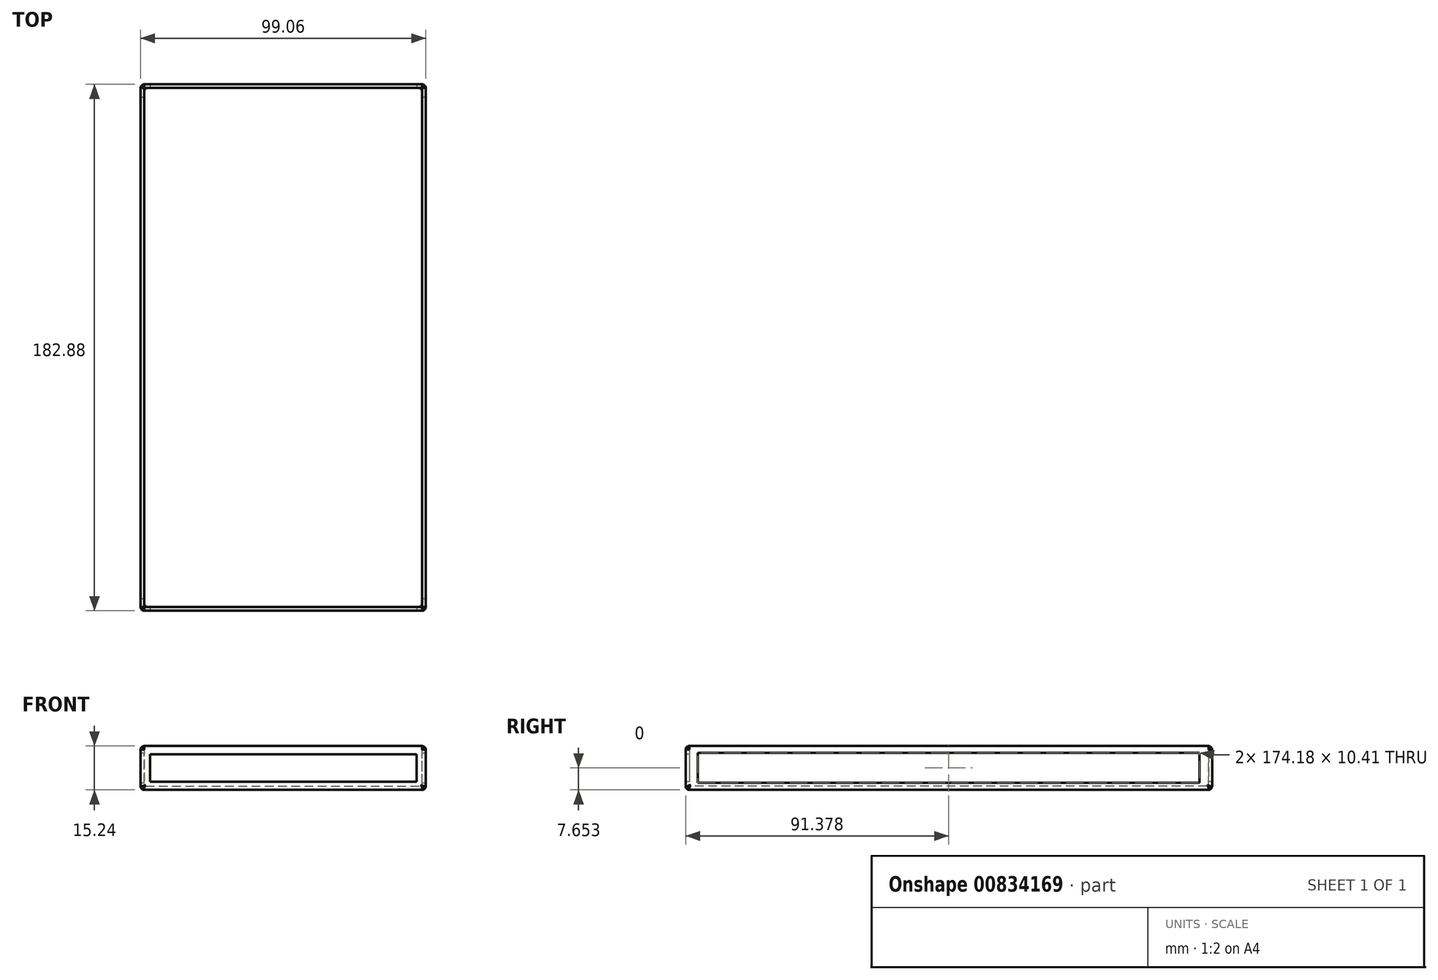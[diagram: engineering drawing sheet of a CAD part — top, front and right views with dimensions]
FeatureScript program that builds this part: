
annotation { "Feature Type Name" : "Feature", "Feature Type Description" : "" }
export const myFeature = defineFeature(function(context is Context, id is Id, definition is map)
    precondition{}
    {
        {
            var Q0;
            Q0=qCreatedBy(makeId("Top.planeOp"),FACE);
            var sketch = newSketch(context, id + "F0", { "sketchPlane" : qUnion([Q0])});
            skLineSegment(sketch, "E0.bottom", {"start": v(-49.53, 91.44) * mm, "end": v(49.53, 91.44) * mm, "construction": true});
            skLineSegment(sketch, "E0.top", {"start": v(-49.53, -91.44) * mm, "end": v(49.53, -91.44) * mm, "construction": true});
            skLineSegment(sketch, "E0.left", {"start": v(-49.53, 91.44) * mm, "end": v(-49.53, -91.44) * mm, "construction": true});
            skLineSegment(sketch, "E0.right", {"start": v(49.53, 91.44) * mm, "end": v(49.53, -91.44) * mm, "construction": true});
            skPoint(sketch, "E0.middle", {"position": v(0, 0) * mm});
            skSolve(sketch);
        }
        {
            var Q0;
            Q0=qCreatedBy(makeId("Top.planeOp"),FACE);
            var sketch = newSketch(context, id + "F1", { "sketchPlane" : qUnion([Q0])});
            skLineSegment(sketch, "E1.bottom", {"start": v(-49.53, 91.44) * mm, "end": v(49.53, 91.44) * mm});
            skLineSegment(sketch, "E1.top", {"start": v(-49.53, -91.44) * mm, "end": v(49.53, -91.44) * mm});
            skLineSegment(sketch, "E1.left", {"start": v(-49.53, 91.44) * mm, "end": v(-49.53, -91.44) * mm});
            skLineSegment(sketch, "E1.right", {"start": v(49.53, 91.44) * mm, "end": v(49.53, -91.44) * mm});
            skSolve(sketch);
        }
        {
            var Q0;
            Q0=qSketchRegion(id+"F1",true);
            extrude(context, id + "F2", {"entities" : qUnion([Q0]), "depth" : 15.24 * mm});
        }
        {
            var Q0;
            Q0=makeQuery(id+"F2.opExtrude","CAP_FACE",FACE,{"disambiguationData":[OSD([sQuery(id+"F1.wireOp",EDGE,"E1.bottom"),sQuery(id+"F1.wireOp",EDGE,"E1.top"),sQuery(id+"F1.wireOp",EDGE,"E1.left"),sQuery(id+"F1.wireOp",EDGE,"E1.right")])],"isStart":false});
            shell(context, id + "F3", {"entities" : qUnion([Q0]), "thickness" : 1.27 * mm});
        }
        {
            var Q0;
            Q0=makeQuery(id+"F2.opExtrude","SWEPT_EDGE",EDGE,{"disambiguationData":[OSD([sQuery(id+"F1.wireOp",EDGE,"E1.bottom"),sQuery(id+"F1.wireOp",EDGE,"E1.right")])]});
            var Q1;
            Q1=makeQuery(id+"F2.opExtrude","SWEPT_EDGE",EDGE,{"disambiguationData":[OSD([sQuery(id+"F1.wireOp",EDGE,"E1.bottom"),sQuery(id+"F1.wireOp",EDGE,"E1.left")])]});
            var Q2;
            Q2=makeQuery(id+"F2.opExtrude","SWEPT_EDGE",EDGE,{"disambiguationData":[OSD([sQuery(id+"F1.wireOp",EDGE,"E1.top"),sQuery(id+"F1.wireOp",EDGE,"E1.left")])]});
            var Q3;
            Q3=makeQuery(id+"F2.opExtrude","SWEPT_EDGE",EDGE,{"disambiguationData":[OSD([sQuery(id+"F1.wireOp",EDGE,"E1.top"),sQuery(id+"F1.wireOp",EDGE,"E1.right")])]});
            var Q4;
            Q4=makeQuery(id+"F2.opExtrude","CAP_EDGE",EDGE,{"disambiguationData":[OSD([sQuery(id+"F1.wireOp",EDGE,"E1.top")])],"isStart":true});
            var Q5;
            Q5=makeQuery(id+"F2.opExtrude","CAP_EDGE",EDGE,{"disambiguationData":[OSD([sQuery(id+"F1.wireOp",EDGE,"E1.right")])],"isStart":true});
            var Q6;
            Q6=makeQuery(id+"F2.opExtrude","CAP_EDGE",EDGE,{"disambiguationData":[OSD([sQuery(id+"F1.wireOp",EDGE,"E1.bottom")])],"isStart":true});
            var Q7;
            Q7=makeQuery(id+"F2.opExtrude","CAP_EDGE",EDGE,{"disambiguationData":[OSD([sQuery(id+"F1.wireOp",EDGE,"E1.left")])],"isStart":true});
            var Q8;
            Q8=makeQuery(id+"F2.opExtrude","CAP_EDGE",EDGE,{"disambiguationData":[OSD([sQuery(id+"F1.wireOp",EDGE,"E1.bottom")])],"isStart":false});
            var Q9;
            Q9=makeQuery(id+"F2.opExtrude","CAP_EDGE",EDGE,{"disambiguationData":[OSD([sQuery(id+"F1.wireOp",EDGE,"E1.left")])],"isStart":false});
            var Q10;
            Q10=makeQuery(id+"F2.opExtrude","CAP_EDGE",EDGE,{"disambiguationData":[OSD([sQuery(id+"F1.wireOp",EDGE,"E1.right")])],"isStart":false});
            var Q11;
            Q11=makeQuery(id+"F2.opExtrude","CAP_EDGE",EDGE,{"disambiguationData":[OSD([sQuery(id+"F1.wireOp",EDGE,"E1.top")])],"isStart":false});
            fillet(context, id + "F4", {"entities" : qUnion([Q0, Q1, Q2, Q3, Q4, Q5, Q6, Q7, Q8, Q9, Q10, Q11]), "radius" : 1.27 * mm, "tangentPropagation" : true, "rho" : 0.4, "crossSection" : FilletCrossSection.CONIC, "allowEdgeOverflow" : false});
        }
        {
            var Q0;
            Q0=makeQuery(id+"F2.opExtrude","SWEPT_FACE",FACE,{"disambiguationData":[OSD([sQuery(id+"F1.wireOp",EDGE,"E1.right")])]});
            var sketch = newSketch(context, id + "F5", { "sketchPlane" : qUnion([Q0])});
            skLineSegment(sketch, "E2.bottom", {"start": v(-87.15, 2.45) * mm, "end": v(87.03, 2.45) * mm});
            skLineSegment(sketch, "E2.top", {"start": v(-87.15, 12.86) * mm, "end": v(87.03, 12.86) * mm});
            skLineSegment(sketch, "E2.left", {"start": v(-87.15, 2.45) * mm, "end": v(-87.15, 12.86) * mm});
            skLineSegment(sketch, "E2.right", {"start": v(87.03, 2.45) * mm, "end": v(87.03, 12.86) * mm});
            skSolve(sketch);
        }
        {
            var Q0;
            Q0=qSketchRegion(id+"F5",true);
            extrude(context, id + "F6", {"entities" : qUnion([Q0]), "operationType" : NewBodyOperationType.REMOVE, "endBound" : BoundingType.THROUGH_ALL, "oppositeDirection" : true, "depth" : 25.4 * mm});
        }
        {
            var Q0;
            Q0=makeQuery(id+"F2.opExtrude","SWEPT_FACE",FACE,{"disambiguationData":[OSD([sQuery(id+"F1.wireOp",EDGE,"E1.top")])]});
            var sketch = newSketch(context, id + "F7", { "sketchPlane" : qUnion([Q0])});
            skLineSegment(sketch, "E3.bottom", {"start": v(-46.2, 2.86) * mm, "end": v(46.33, 2.86) * mm});
            skLineSegment(sketch, "E3.top", {"start": v(-46.2, 12.4) * mm, "end": v(46.33, 12.4) * mm});
            skLineSegment(sketch, "E3.left", {"start": v(-46.2, 2.86) * mm, "end": v(-46.2, 12.4) * mm});
            skLineSegment(sketch, "E3.right", {"start": v(46.33, 2.86) * mm, "end": v(46.33, 12.4) * mm});
            skSolve(sketch);
        }
        {
            var Q0;
            Q0=qSketchRegion(id+"F7",true);
            extrude(context, id + "F8", {"entities" : qUnion([Q0]), "operationType" : NewBodyOperationType.REMOVE, "endBound" : BoundingType.THROUGH_ALL, "oppositeDirection" : true, "depth" : 25.4 * mm});
        }
        {
            var Q0;
            {var subQ0=sQuery(id+"F1.wireOp",EDGE,"E1.bottom");Q0=makeQuery(id+"F3.opShell","OFFSET_EDGE",EDGE,{"disambiguationData":[OSD([subQ0]),TDD([makeQuery(id+"F2.opExtrude","CAP_EDGE",EDGE,{"disambiguationData":[OSD([subQ0])],"isStart":true})])]});}
            var Q1;
            {var subQ0=sQuery(id+"F1.wireOp",EDGE,"E1.left");Q1=makeQuery(id+"F3.opShell","OFFSET_EDGE",EDGE,{"disambiguationData":[OSD([subQ0]),TDD([makeQuery(id+"F2.opExtrude","CAP_EDGE",EDGE,{"disambiguationData":[OSD([subQ0])],"isStart":true})])]});}
            var Q2;
            {var subQ0=sQuery(id+"F1.wireOp",EDGE,"E1.right");Q2=makeQuery(id+"F3.opShell","OFFSET_EDGE",EDGE,{"disambiguationData":[OSD([subQ0]),TDD([makeQuery(id+"F2.opExtrude","CAP_EDGE",EDGE,{"disambiguationData":[OSD([subQ0])],"isStart":true})])]});}
            var Q3;
            {var subQ0=sQuery(id+"F1.wireOp",EDGE,"E1.top");Q3=makeQuery(id+"F3.opShell","OFFSET_EDGE",EDGE,{"disambiguationData":[OSD([subQ0]),TDD([makeQuery(id+"F2.opExtrude","CAP_EDGE",EDGE,{"disambiguationData":[OSD([subQ0])],"isStart":true})])]});}
            var Q4;
            Q4=makeQuery(id+"F3.opShell","OFFSET_EDGE",EDGE,{"disambiguationData":[OSD([sQuery(id+"F1.wireOp",EDGE,"E1.top"),sQuery(id+"F1.wireOp",EDGE,"E1.left")])]});
            var Q5;
            Q5=makeQuery(id+"F3.opShell","OFFSET_EDGE",EDGE,{"disambiguationData":[OSD([sQuery(id+"F1.wireOp",EDGE,"E1.bottom"),sQuery(id+"F1.wireOp",EDGE,"E1.left")])]});
            var Q6;
            Q6=makeQuery(id+"F3.opShell","OFFSET_EDGE",EDGE,{"disambiguationData":[OSD([sQuery(id+"F1.wireOp",EDGE,"E1.bottom"),sQuery(id+"F1.wireOp",EDGE,"E1.right")])]});
            var Q7;
            Q7=makeQuery(id+"F3.opShell","OFFSET_EDGE",EDGE,{"disambiguationData":[OSD([sQuery(id+"F1.wireOp",EDGE,"E1.top"),sQuery(id+"F1.wireOp",EDGE,"E1.right")])]});
            fillet(context, id + "F9", {"entities" : qUnion([Q0, Q1, Q2, Q3, Q4, Q5, Q6, Q7]), "radius" : 0.5 * mm, "tangentPropagation" : true, "rho" : 0.5, "crossSection" : FilletCrossSection.CONIC, "allowEdgeOverflow" : false});
        }
    });
